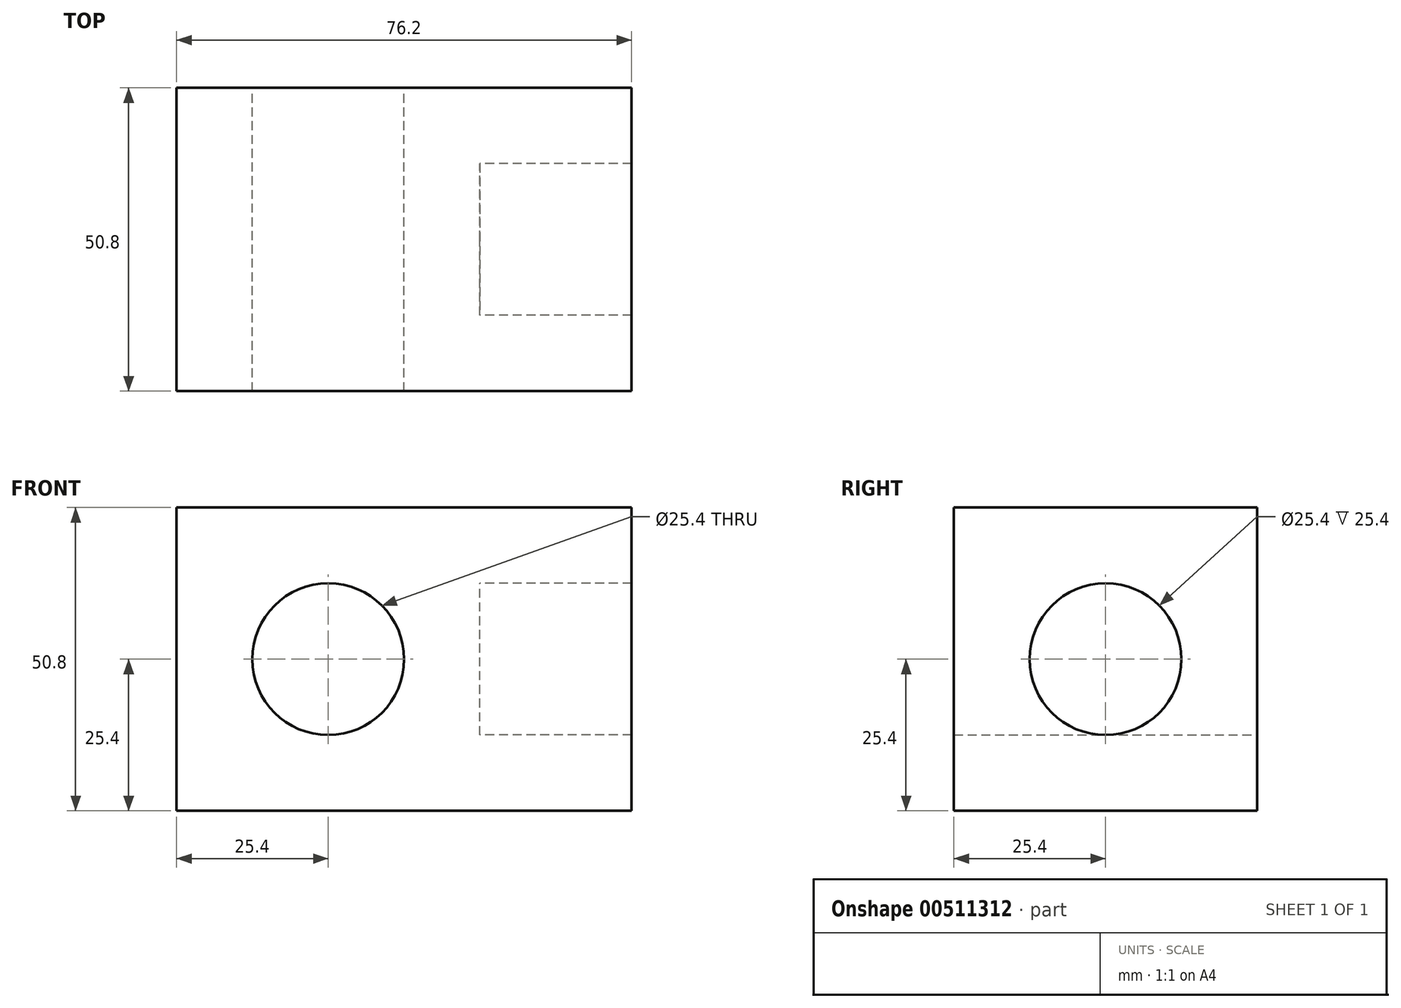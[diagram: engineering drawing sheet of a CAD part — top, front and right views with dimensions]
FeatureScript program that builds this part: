
annotation { "Feature Type Name" : "Feature", "Feature Type Description" : "" }
export const myFeature = defineFeature(function(context is Context, id is Id, definition is map)
    precondition{}
    {
        {
            var Q0;
            Q0=qCreatedBy(makeId("Front.planeOp"),FACE);
            var sketch = newSketch(context, id + "F0", { "sketchPlane" : qUnion([Q0])});
            skLineSegment(sketch, "E0", {"start": v(0, 0) * mm, "end": v(0, 50.8) * mm});
            skLineSegment(sketch, "E1", {"start": v(0, 50.8) * mm, "end": v(50.8, 50.8) * mm});
            skLineSegment(sketch, "E2", {"start": v(50.8, 50.8) * mm, "end": v(50.8, 0) * mm});
            skLineSegment(sketch, "E3", {"start": v(50.8, 0) * mm, "end": v(0, 0) * mm});
            skCircle(sketch, "E4", {"center": v(25.4, 25.4) * mm, "radius": 12.7 * mm});
            skSolve(sketch);
        }
        {
            var Q0;
            Q0 = qSketchRegion(id + "F0", true);
            extrude(context, id + "F1", {"entities" : qUnion([Q0]), "depth" : 50.8 * mm, "offsetDistance" : 25.4 * mm});
        }
        {
            var Q0;
            Q0=makeQuery(id+"F1.opExtrude","SWEPT_FACE",FACE,{"disambiguationData":[OSD([sQuery(id+"F0.wireOp",EDGE,"E2")])]});
            var sketch = newSketch(context, id + "F2", { "sketchPlane" : qUnion([Q0])});
            skCircle(sketch, "E5", {"center": v(-25.4, 25.4) * mm, "radius": 12.7 * mm});
            skSolve(sketch);
        }
        {
            var Q0;
            Q0=makeQuery(id+"F2.imprint","IMPRINT",FACE,{"disambiguationData":[TD([[makeQuery(id+"F2.imprint","IMPRINT",EDGE,{"derivedFrom":sQuery(id+"F2.wireOp",EDGE,"E5")}),-1.0]])]});
            extrude(context, id + "F3", {"entities" : qUnion([Q0]), "operationType" : NewBodyOperationType.ADD, "depth" : 25.4 * mm, "offsetDistance" : 25.4 * mm});
        }
    });
